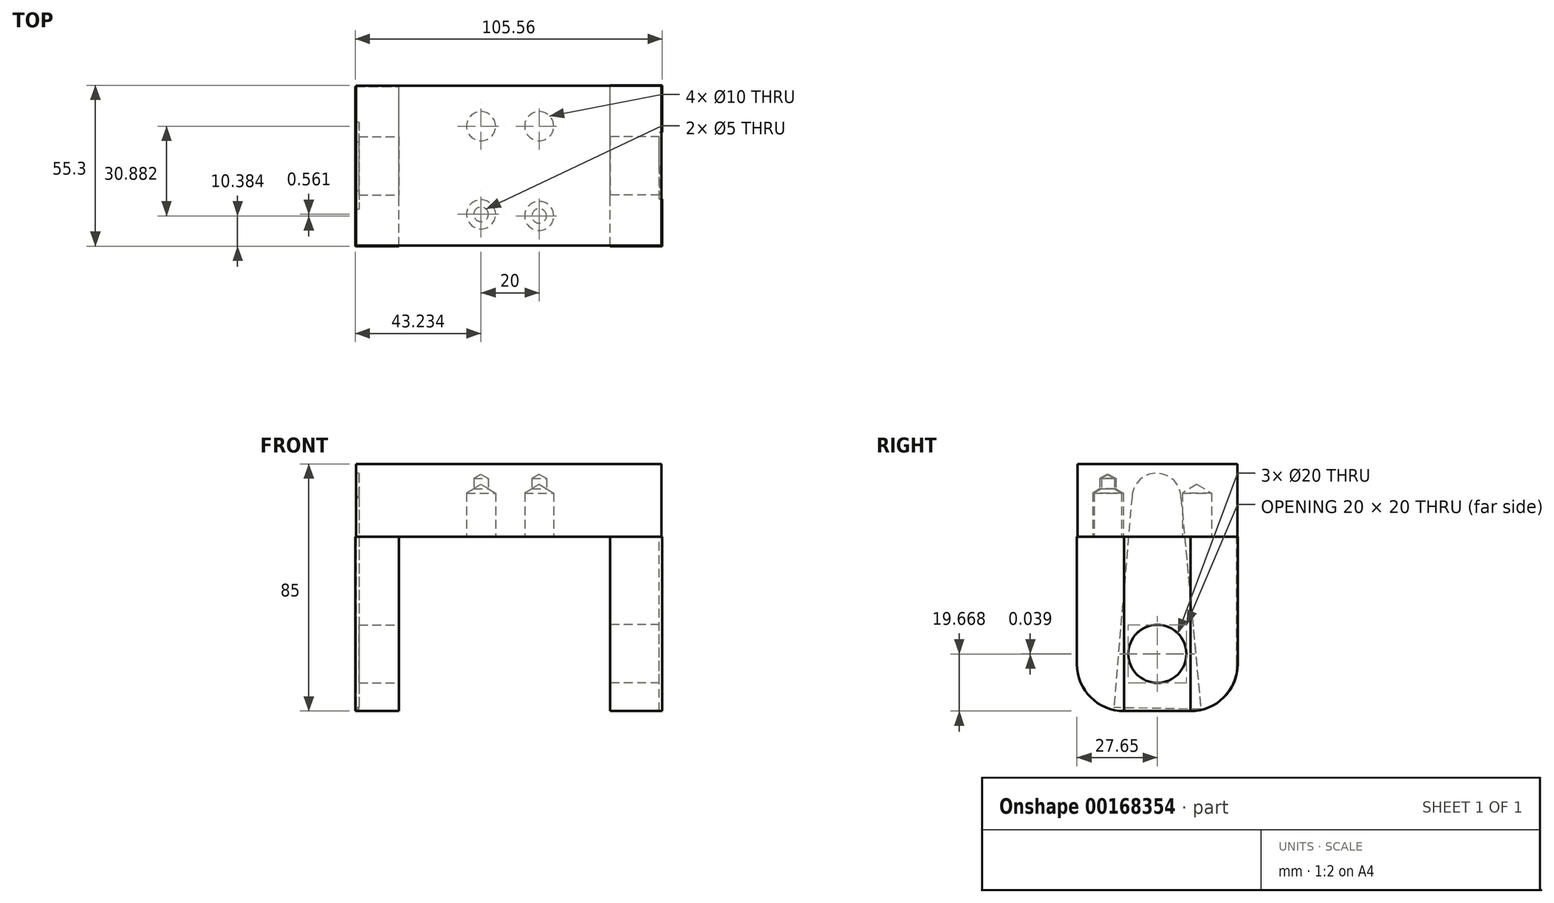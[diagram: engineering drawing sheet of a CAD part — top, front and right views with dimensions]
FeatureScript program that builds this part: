
annotation { "Feature Type Name" : "Feature", "Feature Type Description" : "" }
export const myFeature = defineFeature(function(context is Context, id is Id, definition is map)
    precondition{}
    {
        {
            var Q0;
            Q0=qCreatedBy(makeId("Top.planeOp"),FACE);
            var sketch = newSketch(context, id + "F0", { "sketchPlane" : qUnion([Q0])});
            skLineSegment(sketch, "E0.bottom", {"start": v(-52.5, 27.5) * mm, "end": v(52.5, 27.5) * mm});
            skLineSegment(sketch, "E0.top", {"start": v(-52.5, -27.5) * mm, "end": v(52.5, -27.5) * mm});
            skLineSegment(sketch, "E0.left", {"start": v(-52.5, 27.5) * mm, "end": v(-52.5, -27.5) * mm});
            skLineSegment(sketch, "E0.right", {"start": v(52.5, 27.5) * mm, "end": v(52.5, -27.5) * mm});
            skPoint(sketch, "E0.middle", {"position": v(0, 0) * mm});
            skPoint(sketch, "E1", {"position": v(-9.55, 13.62) * mm});
            skPoint(sketch, "E2", {"position": v(10.45, 13.62) * mm});
            skPoint(sketch, "E3", {"position": v(10.45, -17.27) * mm});
            skPoint(sketch, "E4", {"position": v(-9.55, -16.7) * mm});
            skSolve(sketch);
        }
        {
            var Q0;
            Q0=makeQuery(id+"F0.imprint","IMPRINT",FACE,{"disambiguationData":[TD([[makeQuery(id+"F0.imprint","IMPRINT",EDGE,{"derivedFrom":sQuery(id+"F0.wireOp",EDGE,"E0.bottom")}),-1.0]])]});
            extrude(context, id + "F1", {"entities" : qUnion([Q0]), "depth" : 25 * mm});
        }
        {
            var Q0;
            Q0=sQuery(id+"F0.wireOp",VERTEX,"E1");
            var Q1;
            Q1=sQuery(id+"F0.wireOp",VERTEX,"E4");
            var Q2;
            Q2=sQuery(id+"F0.wireOp",VERTEX,"E2");
            var Q3;
            Q3=sQuery(id+"F0.wireOp",VERTEX,"E3");
            var Q4;
            Q4=makeQuery(id+"F1.opExtrude","SWEPT_BODY",BODY,{"disambiguationData":[OSD([sQuery(id+"F0.wireOp",EDGE,"E0.bottom"),sQuery(id+"F0.wireOp",EDGE,"E0.top"),sQuery(id+"F0.wireOp",EDGE,"E0.left"),sQuery(id+"F0.wireOp",EDGE,"E0.right")])]});
            hole(context, id + "F2", {"style" : HoleStyle.SIMPLE, "endStyle" : HoleEndStyle.BLIND, "oppositeDirection" : true, "holeDiameter" : 10 * mm, "holeDepth" : 15 * mm, "startFromSketch" : true, "locations" : qUnion([Q0, Q1, Q2, Q3]), "scope" : qUnion([Q4])});
        }
        {
            var Q0;
            Q0=sQuery(id+"F0.wireOp",VERTEX,"E4");
            var Q1;
            Q1=sQuery(id+"F0.wireOp",VERTEX,"E3");
            var Q2;
            Q2=makeQuery(id+"F1.opExtrude","SWEPT_BODY",BODY,{"disambiguationData":[OSD([sQuery(id+"F0.wireOp",EDGE,"E0.bottom"),sQuery(id+"F0.wireOp",EDGE,"E0.top"),sQuery(id+"F0.wireOp",EDGE,"E0.left"),sQuery(id+"F0.wireOp",EDGE,"E0.right")])]});
            hole(context, id + "F3", {"style" : HoleStyle.SIMPLE, "endStyle" : HoleEndStyle.BLIND, "oppositeDirection" : true, "holeDiameter" : 5 * mm, "holeDepth" : 20 * mm, "startFromSketch" : true, "locations" : qUnion([Q0, Q1]), "scope" : qUnion([Q2])});
        }
        {
            var Q0;
            Q0=makeQuery(id+"F0.imprint","IMPRINT",FACE,{"disambiguationData":[TD([[makeQuery(id+"F0.imprint","IMPRINT",EDGE,{"derivedFrom":sQuery(id+"F0.wireOp",EDGE,"E0.bottom")}),-1.0]])]});
            var sketch = newSketch(context, id + "F4", { "sketchPlane" : qUnion([Q0])});
            skLineSegment(sketch, "E5.bottom", {"start": v(-52.78, -27.65) * mm, "end": v(-37.78, -27.65) * mm});
            skLineSegment(sketch, "E5.top", {"start": v(-52.78, 27.35) * mm, "end": v(-37.78, 27.35) * mm});
            skLineSegment(sketch, "E5.left", {"start": v(-52.78, -27.65) * mm, "end": v(-52.78, 27.35) * mm});
            skLineSegment(sketch, "E5.right", {"start": v(-37.78, -27.65) * mm, "end": v(-37.78, 27.35) * mm});
            skLineSegment(sketch, "E6.bottom", {"start": v(52.78, -27.65) * mm, "end": v(34.81, -27.65) * mm});
            skLineSegment(sketch, "E6.top", {"start": v(52.78, 27.65) * mm, "end": v(34.81, 27.65) * mm});
            skLineSegment(sketch, "E6.left", {"start": v(52.78, -27.65) * mm, "end": v(52.78, 27.65) * mm});
            skLineSegment(sketch, "E6.right", {"start": v(34.81, -27.65) * mm, "end": v(34.81, 27.65) * mm});
            skSolve(sketch);
        }
        {
            var Q0;
            Q0 = qSketchRegion(id + "F4", true);
            extrude(context, id + "F5", {"entities" : qUnion([Q0]), "operationType" : NewBodyOperationType.ADD, "oppositeDirection" : true, "depth" : 60 * mm});
        }
        {
            var Q0;
            Q0=makeQuery(id+"F5.opExtrude","CAP_EDGE",EDGE,{"disambiguationData":[OSD([sQuery(id+"F4.wireOp",EDGE,"E5.top")])],"isStart":false});
            var Q1;
            Q1=makeQuery(id+"F5.opExtrude","CAP_EDGE",EDGE,{"disambiguationData":[OSD([sQuery(id+"F4.wireOp",EDGE,"E5.bottom")])],"isStart":false});
            var Q2;
            Q2=makeQuery(id+"F5.opExtrude","CAP_EDGE",EDGE,{"disambiguationData":[OSD([sQuery(id+"F4.wireOp",EDGE,"E6.bottom")])],"isStart":false});
            var Q3;
            Q3=makeQuery(id+"F5.opExtrude","CAP_EDGE",EDGE,{"disambiguationData":[OSD([sQuery(id+"F4.wireOp",EDGE,"E6.top")])],"isStart":false});
            fillet(context, id + "F6", {"entities" : qUnion([Q0, Q1, Q2, Q3]), "radius" : 16.18 * mm, "tangentPropagation" : true, "allowEdgeOverflow" : false});
        }
        {
            var Q0;
            Q0=makeQuery(id+"F5.opExtrude","SWEPT_FACE",FACE,{"disambiguationData":[OSD([sQuery(id+"F4.wireOp",EDGE,"E6.right")])]});
            var sketch = newSketch(context, id + "F7", { "sketchPlane" : qUnion([Q0])});
            skPoint(sketch, "E7", {"position": v(0, -40.3) * mm});
            skSolve(sketch);
        }
        {
            var Q0;
            Q0=makeQuery(id+"F5.opExtrude","SWEPT_FACE",FACE,{"disambiguationData":[OSD([sQuery(id+"F4.wireOp",EDGE,"E5.right")])]});
            var sketch = newSketch(context, id + "F8", { "sketchPlane" : qUnion([Q0])});
            skPoint(sketch, "E8", {"position": v(0, -40.33) * mm});
            skSolve(sketch);
        }
        {
            var Q0;
            Q0=sQuery(id+"F7.wireOp",VERTEX,"E7");
            var Q1;
            Q1=sQuery(id+"F8.wireOp",VERTEX,"E8");
            var Q2;
            Q2=makeQuery(id+"F1.opExtrude","SWEPT_BODY",BODY,{"disambiguationData":[OSD([sQuery(id+"F0.wireOp",EDGE,"E0.bottom"),sQuery(id+"F0.wireOp",EDGE,"E0.top"),sQuery(id+"F0.wireOp",EDGE,"E0.left"),sQuery(id+"F0.wireOp",EDGE,"E0.right")])]});
            hole(context, id + "F9", {"style" : HoleStyle.SIMPLE, "endStyle" : HoleEndStyle.BLIND, "holeDiameter" : 20 * mm, "holeDepth" : 50 * mm, "startFromSketch" : true, "locations" : qUnion([Q0, Q1]), "scope" : qUnion([Q2])});
        }
        {
            var Q0;
            Q0=makeQuery(id+"F5.opExtrude","SWEPT_FACE",FACE,{"disambiguationData":[OSD([sQuery(id+"F4.wireOp",EDGE,"E6.left")])]});
            var sketch = newSketch(context, id + "F10", { "sketchPlane" : qUnion([Q0])});
            skLineSegment(sketch, "E9.bottom", {"start": v(11.48, -60) * mm, "end": v(-11.48, -60) * mm});
            skLineSegment(sketch, "E9.top", {"start": v(11.48, 0) * mm, "end": v(-11.48, 0) * mm});
            skLineSegment(sketch, "E9.left", {"start": v(11.48, -60) * mm, "end": v(11.48, 0) * mm});
            skLineSegment(sketch, "E9.right", {"start": v(-11.48, -60) * mm, "end": v(-11.48, 0) * mm});
            skSolve(sketch);
        }
        {
            var Q0;
            Q0=makeQuery(id+"F10.imprint","IMPRINT",FACE,{"disambiguationData":[TD([[makeQuery(id+"F10.imprint","IMPRINT",EDGE,{"derivedFrom":sQuery(id+"F10.wireOp",EDGE,"E9.bottom")}),1.0]])]});
            extrude(context, id + "F11", {"entities" : qUnion([Q0]), "operationType" : NewBodyOperationType.REMOVE, "oppositeDirection" : true, "depth" : 1 * mm});
        }
        {
            var Q0;
            Q0=makeQuery(id+"F1.opExtrude","SWEPT_FACE",FACE,{"disambiguationData":[OSD([sQuery(id+"F0.wireOp",EDGE,"E0.left")])]});
            var sketch = newSketch(context, id + "F12", { "sketchPlane" : qUnion([Q0])});
            skArc(sketch, "E10", {"start": v(8.7, 13.9) * mm, "mid": v(0, 21.83) * mm, "end": v(-8.14, 13.34) * mm});
            skLineSegment(sketch, "E11", {"start": v(-8.14, 13.34) * mm, "end": v(-15, -59.38) * mm});
            skLineSegment(sketch, "E12", {"start": v(8.7, 13.9) * mm, "end": v(15, -58.82) * mm});
            skLineSegment(sketch, "E13", {"start": v(-15, -59.38) * mm, "end": v(15, -58.82) * mm});
            skLineSegment(sketch, "E14", {"start": v(8.7, 13.9) * mm, "end": v(-8.14, 13.34) * mm});
            skSolve(sketch);
        }
        {
            var Q0;
            Q0 = qSketchRegion(id + "F12", true);
            extrude(context, id + "F13", {"entities" : qUnion([Q0]), "operationType" : NewBodyOperationType.REMOVE, "oppositeDirection" : true, "depth" : 1 * mm});
        }
    });
